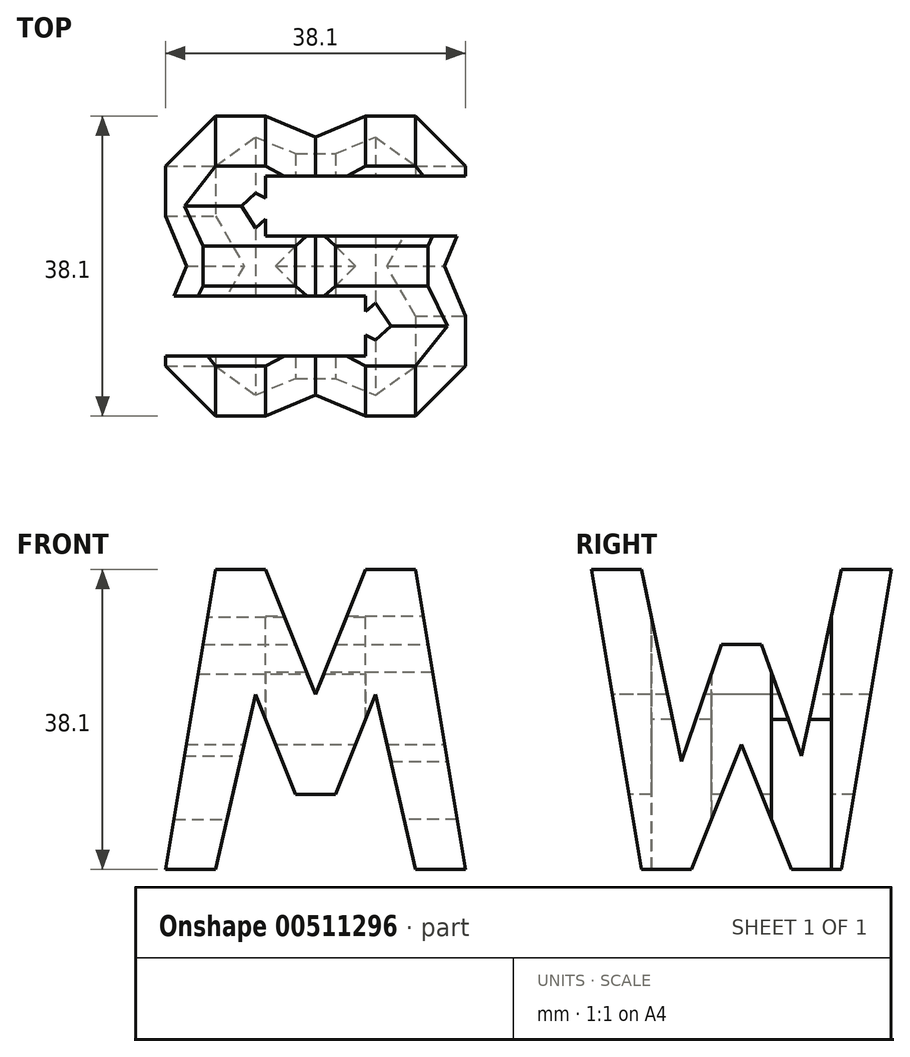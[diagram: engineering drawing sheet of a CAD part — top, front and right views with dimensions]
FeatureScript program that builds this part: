
annotation { "Feature Type Name" : "Feature", "Feature Type Description" : "" }
export const myFeature = defineFeature(function(context is Context, id is Id, definition is map)
    precondition{}
    {
        {
            var Q0;
            Q0=qCreatedBy(makeId("Front.planeOp"),FACE);
            var sketch = newSketch(context, id + "F0", { "sketchPlane" : qUnion([Q0])});
            skLineSegment(sketch, "E0", {"start": v(0, 0) * mm, "end": v(0, 38.1) * mm});
            skLineSegment(sketch, "E1", {"start": v(0, 38.1) * mm, "end": v(38.1, 38.1) * mm});
            skLineSegment(sketch, "E2", {"start": v(38.1, 38.1) * mm, "end": v(38.1, 0) * mm});
            skLineSegment(sketch, "E3", {"start": v(38.1, 0) * mm, "end": v(0, 0) * mm});
            skLineSegment(sketch, "E4", {"start": v(12.7, 38.1) * mm, "end": v(19.05, 22.23) * mm});
            skLineSegment(sketch, "E5", {"start": v(19.05, 22.23) * mm, "end": v(25.4, 38.1) * mm});
            skPoint(sketch, "E6.start.orphan", {"position": v(14.79, 9.53) * mm});
            skLineSegment(sketch, "E7", {"start": v(6.35, 0) * mm, "end": v(11.43, 22.22) * mm});
            skLineSegment(sketch, "E8", {"start": v(11.43, 22.22) * mm, "end": v(16.51, 9.52) * mm});
            skLineSegment(sketch, "E9", {"start": v(16.51, 9.53) * mm, "end": v(21.6, 9.53) * mm});
            skLineSegment(sketch, "E10", {"start": v(21.59, 9.53) * mm, "end": v(26.67, 22.23) * mm});
            skLineSegment(sketch, "E11", {"start": v(26.67, 22.23) * mm, "end": v(31.75, 0) * mm});
            skPoint(sketch, "E12.end.orphan", {"position": v(6.35, 38.1) * mm});
            skLineSegment(sketch, "E13", {"start": v(6.35, 38.1) * mm, "end": v(0, 0) * mm});
            skPoint(sketch, "E14.start.orphan", {"position": v(31.75, 38.1) * mm});
            skLineSegment(sketch, "E15", {"start": v(31.75, 38.1) * mm, "end": v(38.1, 0) * mm});
            skSolve(sketch);
        }
        {
            var Q0;
            Q0 = qSketchRegion(id + "F0", true);
            extrude(context, id + "F1", {"entities" : qUnion([Q0]), "oppositeDirection" : true, "depth" : 38.1 * mm, "offsetDistance" : 25.4 * mm});
        }
        {
            var Q0;
            Q0=qCreatedBy(makeId("Front.planeOp"),FACE);
            cPlane(context, id + "F2", {"entities" : qUnion([Q0]), "cplaneType" : CPlaneType.OFFSET, "offset" : 38.1 * mm, "oppositeDirection" : true, "width" : 152.4 * mm, "height" : 152.4 * mm});
        }
        {
            var Q0;
            Q0=qCreatedBy(makeId("Right.planeOp"),FACE);
            cPlane(context, id + "F3", {"entities" : qUnion([Q0]), "cplaneType" : CPlaneType.OFFSET, "offset" : 38.1 * mm, "width" : 152.4 * mm, "height" : 152.4 * mm});
        }
        {
            var Q0;
            Q0=qCreatedBy(makeId("Top.planeOp"),FACE);
            cPlane(context, id + "F4", {"entities" : qUnion([Q0]), "cplaneType" : CPlaneType.OFFSET, "offset" : 38.1 * mm, "width" : 152.4 * mm, "height" : 152.4 * mm});
        }
        {
            var Q0;
            Q0=qCreatedBy(id+"F3.planeOp",FACE);
            var sketch = newSketch(context, id + "F5", { "sketchPlane" : qUnion([Q0])});
            skLineSegment(sketch, "E16", {"start": v(0, 0) * mm, "end": v(0, 38.1) * mm});
            skLineSegment(sketch, "E17", {"start": v(0, 38.1) * mm, "end": v(38.1, 38.1) * mm});
            skLineSegment(sketch, "E18", {"start": v(38.1, 38.1) * mm, "end": v(38.1, 0) * mm});
            skLineSegment(sketch, "E19", {"start": v(38.1, 0) * mm, "end": v(0, 0) * mm});
            skLineSegment(sketch, "E20", {"start": v(0, 38.1) * mm, "end": v(6.35, 0) * mm});
            skLineSegment(sketch, "E21", {"start": v(38.1, 38.1) * mm, "end": v(31.75, 0) * mm});
            skLineSegment(sketch, "E22", {"start": v(6.35, 38.1) * mm, "end": v(11.43, 13.7) * mm});
            skLineSegment(sketch, "E23", {"start": v(11.43, 13.7) * mm, "end": v(16.51, 28.57) * mm});
            skLineSegment(sketch, "E24", {"start": v(16.51, 28.57) * mm, "end": v(21.59, 28.57) * mm});
            skLineSegment(sketch, "E25", {"start": v(21.59, 28.57) * mm, "end": v(26.67, 14.42) * mm});
            skLineSegment(sketch, "E26", {"start": v(26.67, 14.42) * mm, "end": v(31.75, 38.1) * mm});
            skLineSegment(sketch, "E27", {"start": v(12.7, 0) * mm, "end": v(19.05, 15.87) * mm});
            skLineSegment(sketch, "E28", {"start": v(19.05, 15.88) * mm, "end": v(25.4, 0) * mm});
            skPoint(sketch, "E29", {"position": v(19.05, 15.87) * mm});
            skLineSegment(sketch, "E30", {"start": v(0, 0) * mm, "end": v(38.1, 0) * mm});
            skSolve(sketch);
        }
        {
            var Q0;
            {var subQ0=sQuery(id+"F5.wireOp",EDGE,"E22");Q0=makeQuery(id+"F5.imprint","IMPRINT",FACE,{"disambiguationData":[TD([[makeQuery(id+"F5.imprint","IMPRINT",EDGE,{"derivedFrom":subQ0}),1.0]])]});}
            var Q1;
            {var subQ0=sQuery(id+"F5.wireOp",EDGE,"E16");Q1=makeQuery(id+"F5.imprint","IMPRINT",FACE,{"disambiguationData":[TD([[makeQuery(id+"F5.imprint","IMPRINT",EDGE,{"derivedFrom":subQ0}),-1.0]])]});}
            var Q2;
            {var subQ0=sQuery(id+"F5.wireOp",EDGE,"E27");Q2=makeQuery(id+"F5.imprint","IMPRINT",FACE,{"disambiguationData":[TD([[makeQuery(id+"F5.imprint","IMPRINT",EDGE,{"derivedFrom":subQ0}),-1.0]])]});}
            var Q3;
            {var subQ0=sQuery(id+"F5.wireOp",EDGE,"E18");Q3=makeQuery(id+"F5.imprint","IMPRINT",FACE,{"disambiguationData":[TD([[makeQuery(id+"F5.imprint","IMPRINT",EDGE,{"derivedFrom":subQ0}),-1.0]])]});}
            extrude(context, id + "F6", {"entities" : qUnion([Q0, Q1, Q2, Q3]), "operationType" : NewBodyOperationType.REMOVE, "oppositeDirection" : true, "depth" : 38.1 * mm, "offsetDistance" : 25.4 * mm});
        }
        {
            var Q0;
            {var subQ0=sQuery(id+"F0.wireOp",EDGE,"E0");Q0=makeQuery(id+"F0.imprint","IMPRINT",FACE,{"disambiguationData":[TD([[makeQuery(id+"F0.imprint","IMPRINT",EDGE,{"derivedFrom":subQ0}),-1.0]])]});}
            var Q1;
            {var subQ0=sQuery(id+"F0.wireOp",EDGE,"E4");Q1=makeQuery(id+"F0.imprint","IMPRINT",FACE,{"disambiguationData":[TD([[makeQuery(id+"F0.imprint","IMPRINT",EDGE,{"derivedFrom":subQ0}),1.0]])]});}
            var Q2;
            {var subQ0=sQuery(id+"F0.wireOp",EDGE,"E2");Q2=makeQuery(id+"F0.imprint","IMPRINT",FACE,{"disambiguationData":[TD([[makeQuery(id+"F0.imprint","IMPRINT",EDGE,{"derivedFrom":subQ0}),-1.0]])]});}
            var Q3;
            {var subQ0=sQuery(id+"F0.wireOp",EDGE,"E7");Q3=makeQuery(id+"F0.imprint","IMPRINT",FACE,{"disambiguationData":[TD([[makeQuery(id+"F0.imprint","IMPRINT",EDGE,{"derivedFrom":subQ0}),-1.0]])]});}
            extrude(context, id + "F7", {"entities" : qUnion([Q0, Q1, Q2, Q3]), "operationType" : NewBodyOperationType.REMOVE, "oppositeDirection" : true, "depth" : 38.1 * mm, "offsetDistance" : 25.4 * mm});
        }
        {
            var Q0;
            Q0=qCreatedBy(id+"F4.planeOp",FACE);
            var sketch = newSketch(context, id + "F8", { "sketchPlane" : qUnion([Q0])});
            skLineSegment(sketch, "E31", {"start": v(0, 0) * mm, "end": v(38.1, 0) * mm});
            skLineSegment(sketch, "E32", {"start": v(38.1, 0) * mm, "end": v(38.1, 38.1) * mm});
            skLineSegment(sketch, "E33", {"start": v(38.1, 38.1) * mm, "end": v(0, 38.1) * mm});
            skLineSegment(sketch, "E34", {"start": v(0, 38.1) * mm, "end": v(0, 0) * mm});
            skLineSegment(sketch, "E35", {"start": v(0, 7.62) * mm, "end": v(25.4, 7.62) * mm});
            skLineSegment(sketch, "E36", {"start": v(25.4, 7.62) * mm, "end": v(25.4, 15.24) * mm});
            skLineSegment(sketch, "E37", {"start": v(25.4, 15.24) * mm, "end": v(0, 15.24) * mm});
            skLineSegment(sketch, "E38", {"start": v(38.1, 30.48) * mm, "end": v(12.7, 30.48) * mm});
            skLineSegment(sketch, "E39", {"start": v(12.7, 30.48) * mm, "end": v(12.7, 22.86) * mm});
            skLineSegment(sketch, "E40", {"start": v(12.7, 22.86) * mm, "end": v(38.1, 22.86) * mm});
            skSolve(sketch);
        }
        {
            var Q0;
            {var subQ0=sQuery(id+"F8.wireOp",EDGE,"E38");Q0=makeQuery(id+"F8.imprint","IMPRINT",FACE,{"disambiguationData":[TD([[makeQuery(id+"F8.imprint","IMPRINT",EDGE,{"derivedFrom":subQ0}),1.0]])]});}
            var Q1;
            {var subQ0=sQuery(id+"F8.wireOp",EDGE,"E35");Q1=makeQuery(id+"F8.imprint","IMPRINT",FACE,{"disambiguationData":[TD([[makeQuery(id+"F8.imprint","IMPRINT",EDGE,{"derivedFrom":subQ0}),1.0]])]});}
            extrude(context, id + "F9", {"entities" : qUnion([Q0, Q1]), "operationType" : NewBodyOperationType.REMOVE, "oppositeDirection" : true, "depth" : 38.1 * mm, "offsetDistance" : 25.4 * mm});
        }
    });
